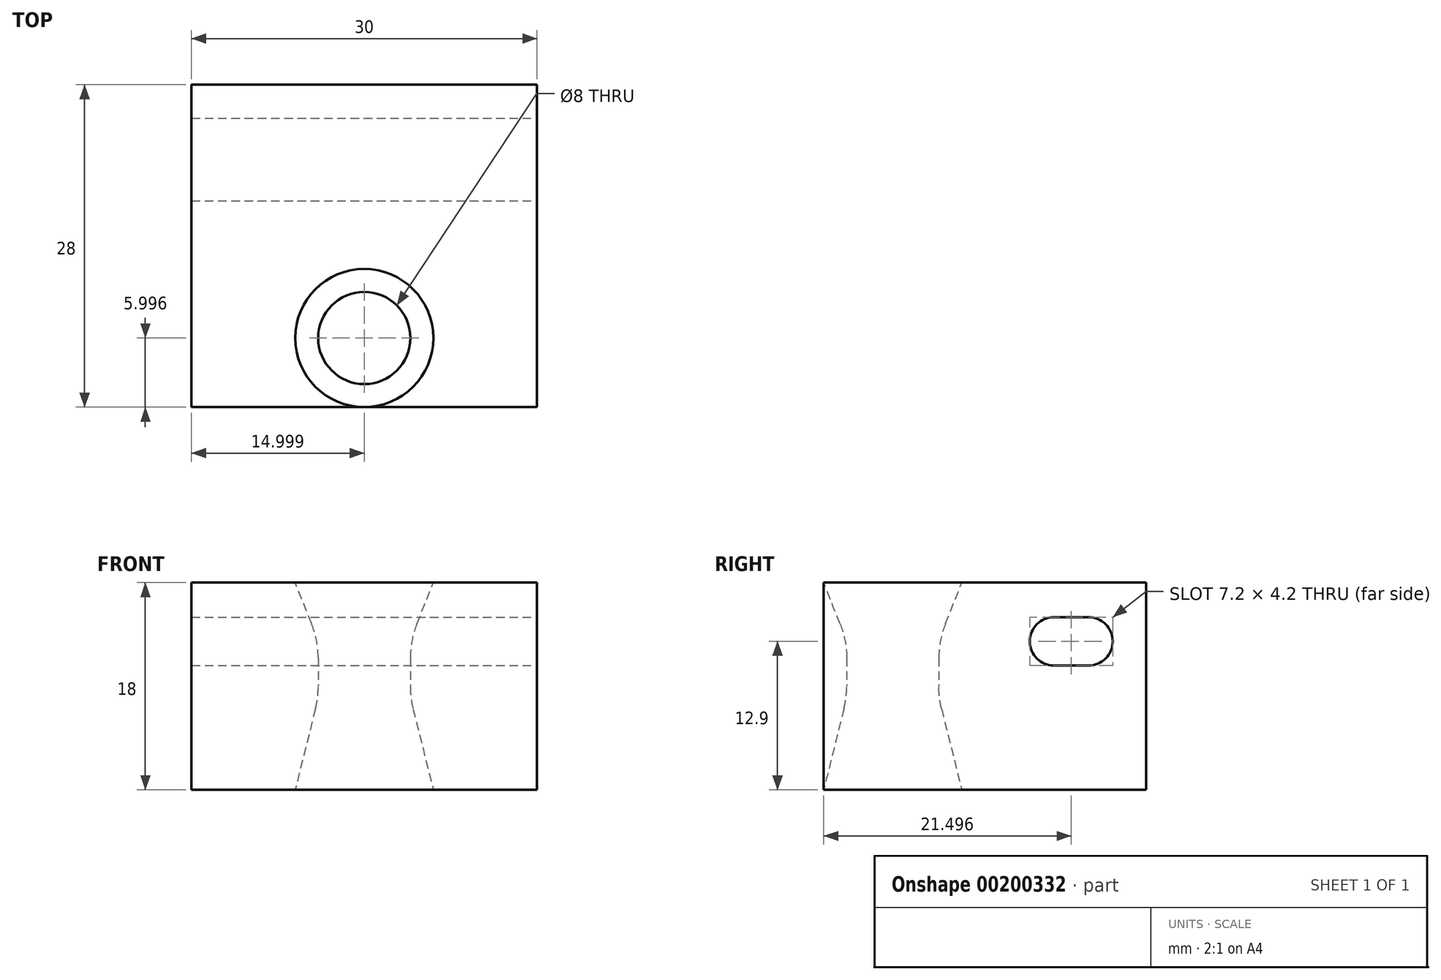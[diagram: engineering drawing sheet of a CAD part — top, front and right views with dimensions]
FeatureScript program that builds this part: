
annotation { "Feature Type Name" : "Feature", "Feature Type Description" : "" }
export const myFeature = defineFeature(function(context is Context, id is Id, definition is map)
    precondition{}
    {
        {
            var Q0;
            Q0=qCreatedBy(makeId("Top.planeOp"),FACE);
            var sketch = newSketch(context, id + "F0", { "sketchPlane" : qUnion([Q0])});
            skLineSegment(sketch, "E0.bottom", {"start": v(-45.4, 26.48) * mm, "end": v(-15.4, 26.48) * mm});
            skLineSegment(sketch, "E0.top", {"start": v(-45.4, -1.52) * mm, "end": v(-15.4, -1.52) * mm});
            skLineSegment(sketch, "E0.left", {"start": v(-45.4, 26.48) * mm, "end": v(-45.4, -1.52) * mm});
            skLineSegment(sketch, "E0.right", {"start": v(-15.4, 26.48) * mm, "end": v(-15.4, -1.52) * mm});
            skLineSegment(sketch, "E1.0", {"start": v(-45.4, 10.48) * mm, "end": v(-15.4, 10.48) * mm, "construction": true});
            skLineSegment(sketch, "E2", {"start": v(-30.4, -1.52) * mm, "end": v(-30.4, 26.48) * mm, "construction": true});
            skLineSegment(sketch, "E3.0", {"start": v(-45.4, 4.48) * mm, "end": v(-15.4, 4.48) * mm, "construction": true});
            skCircle(sketch, "E4", {"center": v(-30.4, 4.48) * mm, "radius": 4 * mm});
            skSolve(sketch);
        }
        {
            var Q0;
            Q0=makeQuery(id+"F0.imprint","IMPRINT",FACE,{"disambiguationData":[TD([[makeQuery(id+"F0.imprint","IMPRINT",EDGE,{"derivedFrom":sQuery(id+"F0.wireOp",EDGE,"E0.bottom")}),-1.0]])]});
            extrude(context, id + "F1", {"entities" : qUnion([Q0]), "depth" : 18 * mm});
        }
        {
            var Q0;
            Q0=makeQuery(id+"F1.opExtrude","CAP_EDGE",EDGE,{"disambiguationData":[OSD([sQuery(id+"F0.wireOp",EDGE,"E4")])],"isStart":true});
            chamfer(context, id + "F2", {"entities" : qUnion([Q0]), "chamferType" : ChamferType.TWO_OFFSETS, "width1" : 2 * mm, "oppositeDirection" : false, "width2" : 8 * mm, "tangentPropagation" : true});
        }
        {
            var Q0;
            Q0=makeQuery(id+"F1.opExtrude","SWEPT_FACE",FACE,{"disambiguationData":[OSD([sQuery(id+"F0.wireOp",EDGE,"E0.right")])]});
            var sketch = newSketch(context, id + "F3", { "sketchPlane" : qUnion([Q0])});
            skLineSegment(sketch, "E5.0", {"start": v(26.48, 12.9) * mm, "end": v(-1.52, 12.9) * mm, "construction": true});
            skLineSegment(sketch, "E6.0", {"start": v(21.48, 18) * mm, "end": v(21.48, 0) * mm, "construction": true});
            skLineSegment(sketch, "E7.0", {"start": v(18.48, 18) * mm, "end": v(18.48, 0) * mm, "construction": true});
            skArc(sketch, "E8", {"start": v(21.48, 10.8) * mm, "mid": v(23.58, 12.9) * mm, "end": v(21.48, 15) * mm});
            skArc(sketch, "E9", {"start": v(20.58, 12.9) * mm, "mid": v(17, 14.38) * mm, "end": v(18.48, 10.8) * mm});
            skLineSegment(sketch, "E10", {"start": v(21.48, 15) * mm, "end": v(18.48, 15) * mm});
            skLineSegment(sketch, "E11", {"start": v(21.48, 10.8) * mm, "end": v(18.48, 10.8) * mm});
            skSolve(sketch);
        }
        {
            var Q0;
            Q0=makeQuery(id+"F3.imprint","IMPRINT",FACE,{"disambiguationData":[TD([[makeQuery(id+"F3.imprint","IMPRINT",EDGE,{"derivedFrom":sQuery(id+"F3.wireOp",EDGE,"E8")}),1.0]])]});
            extrude(context, id + "F4", {"entities" : qUnion([Q0]), "operationType" : NewBodyOperationType.REMOVE, "oppositeDirection" : true, "depth" : 40 * mm});
        }
        {
            var Q0;
            Q0=makeQuery(id+"F1.opExtrude","CAP_EDGE",EDGE,{"disambiguationData":[OSD([sQuery(id+"F0.wireOp",EDGE,"E4")])],"isStart":false});
            chamfer(context, id + "F5", {"entities" : qUnion([Q0]), "chamferType" : ChamferType.TWO_OFFSETS, "width1" : 5 * mm, "oppositeDirection" : false, "width2" : 2 * mm, "tangentPropagation" : true});
        }
        {
            var Q0;
            {var subQ0=sQuery(id+"F0.wireOp",EDGE,"E4");Q0=makeQuery(id+"F5.opChamfer","BLEND_EDGE",EDGE,{"blendedFrom":[makeQuery(id+"F1.opExtrude","CAP_EDGE",EDGE,{"disambiguationData":[OSD([subQ0])],"isStart":false}),makeQuery(id+"F1.opExtrude","SWEPT_FACE",FACE,{"disambiguationData":[OSD([subQ0])]})],"blendedInto":[makeQuery(id+"F1.opExtrude","SWEPT_FACE",FACE,{"disambiguationData":[OSD([subQ0])]})]});}
            fillet(context, id + "F6", {"entities" : qUnion([Q0]), "radius" : 8 * mm, "tangentPropagation" : true, "allowEdgeOverflow" : false});
        }
        {
            var Q0;
            {var subQ0=sQuery(id+"F0.wireOp",EDGE,"E4");Q0=makeQuery(id+"F2.opChamfer","BLEND_EDGE",EDGE,{"blendedFrom":[makeQuery(id+"F1.opExtrude","CAP_EDGE",EDGE,{"disambiguationData":[OSD([subQ0])],"isStart":true}),makeQuery(id+"F1.opExtrude","SWEPT_FACE",FACE,{"disambiguationData":[OSD([subQ0])]})],"blendedInto":[makeQuery(id+"F1.opExtrude","SWEPT_FACE",FACE,{"disambiguationData":[OSD([subQ0])]})]});}
            fillet(context, id + "F7", {"entities" : qUnion([Q0]), "radius" : 8 * mm, "tangentPropagation" : true, "allowEdgeOverflow" : false});
        }
    });
